# Revit family: K11-231FRB-TY5130_Metric
name_source: partatom
category: Sprinklers
units: mm (PartAtom-declared; Revit-internal decimal feet)

## family parameters
Always vertical = Yes
Cut with Voids When Loaded = No
Maintain Annotation Orientation = No
OmniClass Number = 23.65.70.17.11.24
OmniClass Title = Fire Fighting Sprinkler Heads
Part Type = Normal
Room Calculation Point = No
Round Connector Dimension = Use Diameter
Shared = No
Work Plane-Based = No

## types (6) — shared parameters
COBie = No
COBie.Component.Name = Sprinklers:Upright_SIN
COBie.Type = No
COBie.Type.AssetType = Fixed
COBie.Type.Category = Pr_70_55_97_84:Sprinklers
COBie.Type.DurationUnit = year
COBie.Type.Manufacturer = Tyco Fire Protection Products
COBie.Type.Shape = Cylinder
COBie.Type.Size = 3/4"(DN20)
Coverage = Standard
Coverage_ = Standard
K-Factor = 160
Manufacturer = Tyco Fire Protection Products
Manufacturer URL = www.tyco-fire.com
Model = K11-231B
Nominal Diameter 1 = 20 mm
Orifice = Standard
Orifice Size = 16 mm
Outside Diameter 1 = 27 mm
Response = Quick
Response_ = Standard
SIN No = TY5130
Takeout 1 = 62 mm
Technical Data Sheet No = TFP345
zero-valued in all types: COBie.Type.NominalHeight, COBie.Type.NominalLength, COBie.Type.NominalWidth, COBie.Type.ReplacementCost, Default Elevation, Style Id

## per-type parameters (varying)
| type | COBie.Type.Colour | COBie.Type.Finish | COBie.Type.Material | Description | Finish_ | Material_ | Part No | Temperature Rating |
| K11-231B Wet Upright_Brass_155°F/ 68°C_K160_DN20_52-892-1-155 | Yellow | Natural Brass | Bronze | K11-231B Wet Upright_Brass_155°F/ 68°C_K160_DN20_52-894-1-155
K11-231B Wet Upright_Brass_155°F/ 68°C_K160_DN20_52-894-1-155 | Natural Brass | Bronze | 52-892-1-155 | 68 °C |
| K11-231B Wet Upright_Brass_268°F/ 141°C_K160_DN20_52-892-1-286 | Yellow | Natural Brass | Bronze | K11-231B Wet Upright_Brass_155°F/ 68°C_K160_DN20_52-894-1-286
K11-231B Wet Upright_Brass_155°F/ 68°C_K160_DN20_52-894-1-155 | Natural Brass | Bronze | 52-892-1-286 | 141 °C |
| K11-231B Wet Upright_Chrome_200°F/ 93°C_K160_DN20_52-892-9-200 |  |  |  | K11-231B Wet Upright_Chrome_200°F/ 93°C_K160_DN20_52-894-9-200 | Natural Brass | Bronze | 52-892-9-200 | 93 °C |
| K11-231B Wet Upright_Chrome_155°F/ 68°C_K160_DN20_52-892-9-155 | Yellow | Natural Brass | Bronze | K11-231B Wet Upright_Chrome_155°F/ 68°C_K160_DN20_52-894-9-155 | Chrome | Chrome | 52-892-9-155 | 68 °C |
| K11-231B Wet Upright_Chrome_268°F/ 141°C_K160_DN20_52-892-9-286 |  |  |  | K11-231B Wet Upright_Chrome_268°F/ 141°C_K160_DN20_52-894-9-286 | Chrome | Chrome | 52-892-9-286 | 141 °C |
| K11-231B Wet Upright_Brass_200°F/ 93°C_K160_DN20_52-892-1-200 |  |  |  | K11-231B Wet Upright_Brass_200°F/ 93°C_K160_DN20_52-894-1-200 | Natural Brass | Bronze | 52-892-1-200 | 93 °C |

## geometry (parser evidence)
native form markers: Blend x4, Sweep x68
no freeform markers — native parametric forms only
